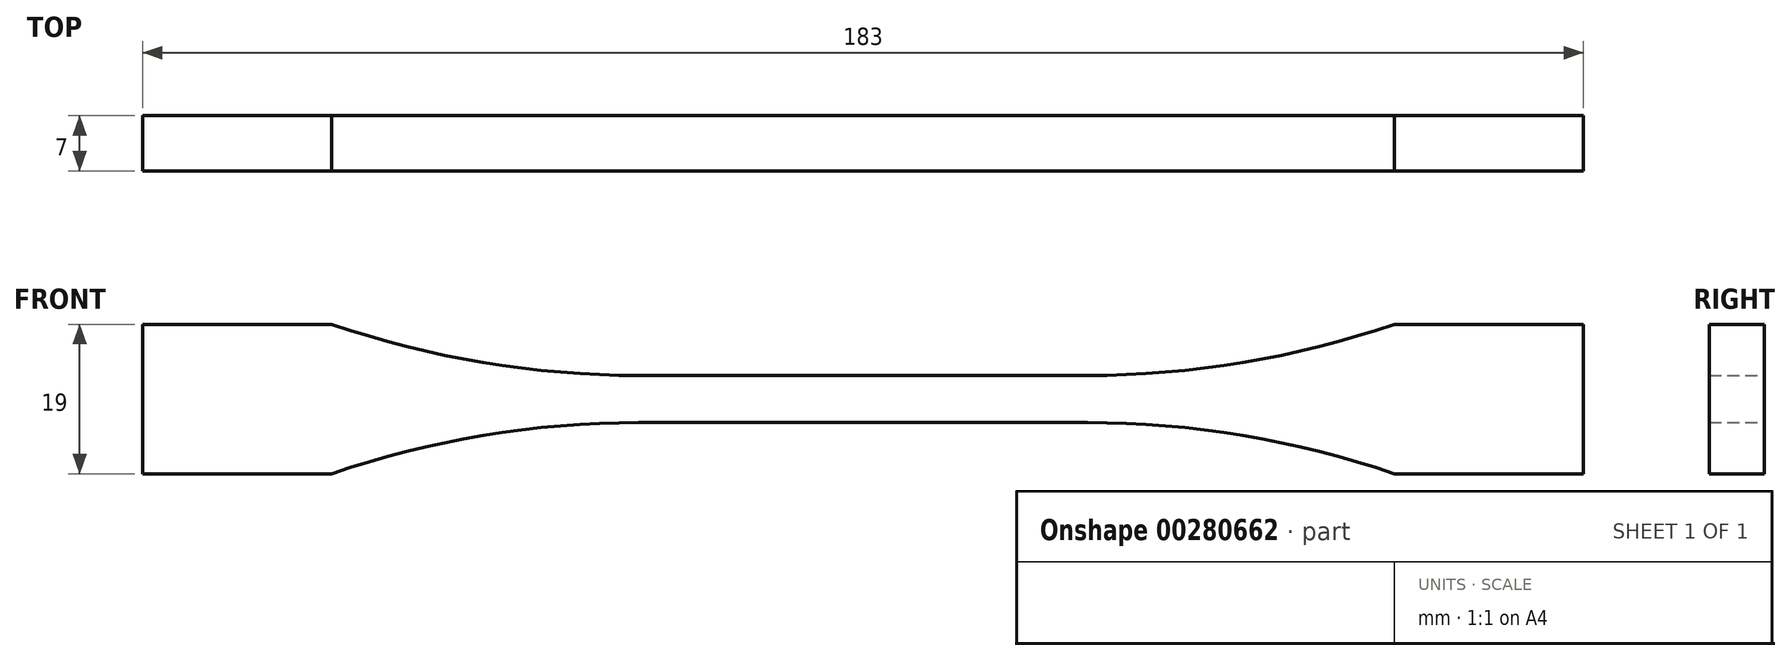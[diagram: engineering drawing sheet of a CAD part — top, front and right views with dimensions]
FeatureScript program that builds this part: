
annotation { "Feature Type Name" : "Feature", "Feature Type Description" : "" }
export const myFeature = defineFeature(function(context is Context, id is Id, definition is map)
    precondition{}
    {
        {
            var Q0;
            Q0=qCreatedBy(makeId("Front.planeOp"),FACE);
            var sketch = newSketch(context, id + "F0", { "sketchPlane" : qUnion([Q0])});
            skLineSegment(sketch, "E0", {"start": v(0, 3) * mm, "end": v(28.5, 3) * mm});
            skArc(sketch, "E1", {"start": v(28.5, 3) * mm, "mid": v(48.27, 4.64) * mm, "end": v(67.5, 9.5) * mm});
            skLineSegment(sketch, "E2", {"start": v(67.5, 9.5) * mm, "end": v(91.5, 9.5) * mm});
            skLineSegment(sketch, "E3", {"start": v(91.5, 9.5) * mm, "end": v(91.5, 0) * mm});
            skLineSegment(sketch, "E4.MirrorCS", {"start": v(-67.5, 9.5) * mm, "end": v(-91.5, 9.5) * mm});
            skArc(sketch, "E5.MirrorCS", {"start": v(-28.5, 3) * mm, "mid": v(-48.27, 4.64) * mm, "end": v(-67.5, 9.5) * mm});
            skLineSegment(sketch, "E6.MirrorCS", {"start": v(-91.5, 9.5) * mm, "end": v(-91.5, 0) * mm});
            skLineSegment(sketch, "E7.MirrorCS", {"start": v(0, 3) * mm, "end": v(-28.5, 3) * mm});
            skLineSegment(sketch, "E8.MirrorCS", {"start": v(0, -3) * mm, "end": v(-28.5, -3) * mm});
            skLineSegment(sketch, "E9.MirrorCS", {"start": v(-91.5, -9.5) * mm, "end": v(-91.5, 0) * mm});
            skLineSegment(sketch, "E10.MirrorCS", {"start": v(0, -3) * mm, "end": v(28.5, -3) * mm});
            skArc(sketch, "E11.MirrorCS", {"start": v(28.5, -3) * mm, "mid": v(48.27, -4.64) * mm, "end": v(67.5, -9.5) * mm});
            skLineSegment(sketch, "E12.MirrorCS", {"start": v(67.5, -9.5) * mm, "end": v(91.5, -9.5) * mm});
            skLineSegment(sketch, "E13.MirrorCS", {"start": v(-67.5, -9.5) * mm, "end": v(-91.5, -9.5) * mm});
            skArc(sketch, "E14.MirrorCS", {"start": v(-28.5, -3) * mm, "mid": v(-48.27, -4.64) * mm, "end": v(-67.5, -9.5) * mm});
            skLineSegment(sketch, "E15.MirrorCS", {"start": v(91.5, -9.5) * mm, "end": v(91.5, 0) * mm});
            skSolve(sketch);
        }
        {
            var Q0;
            Q0 = qSketchRegion(id + "F0", true);
            extrude(context, id + "F1", {"entities" : qUnion([Q0]), "endBound" : BoundingType.SYMMETRIC, "depth" : 7 * mm});
        }
    });
